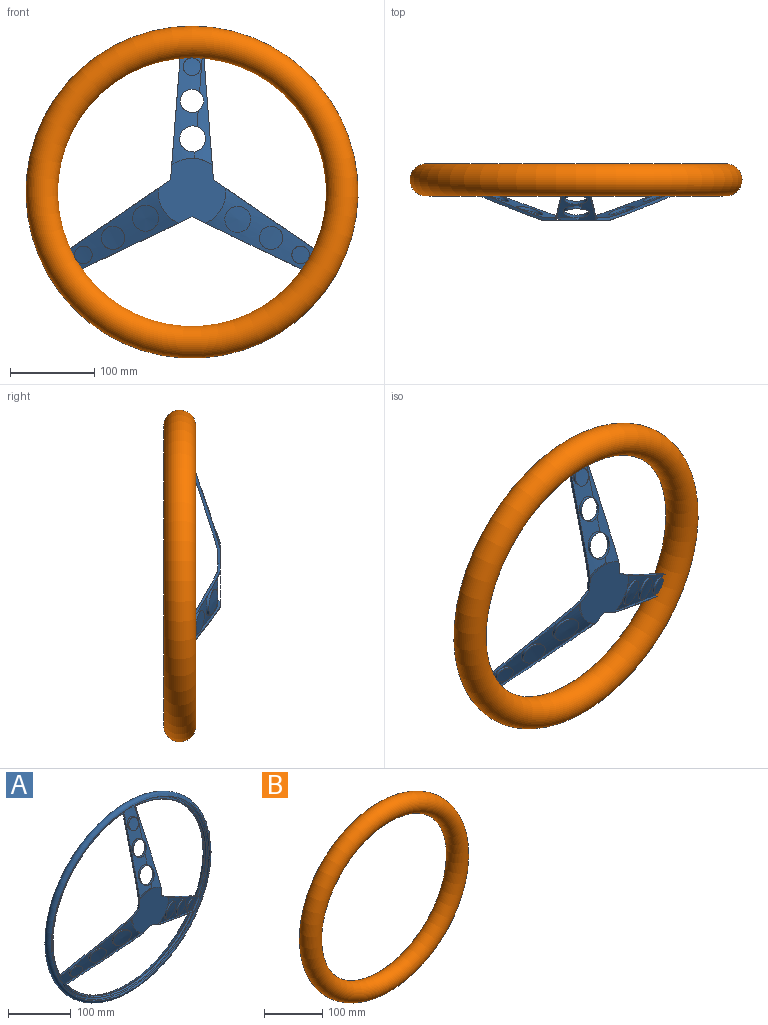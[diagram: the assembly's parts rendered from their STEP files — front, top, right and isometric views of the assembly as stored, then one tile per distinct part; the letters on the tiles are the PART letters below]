
ASSEMBLY  parts=2 mates=1
PART A: 36 faces, bbox 399.2x57.2x399.2 mm
  f0: cone r=178.42mm half-angle=70.8deg, axis (0,1,0), area 1142.8mm2, adj f1,f2,f3,f4,f5,f6
  f1: cone r=183.59mm half-angle=4.7deg, axis (0,-1,0), area 4385.1mm2, adj f0,f7
  f2: cone r=178.42mm half-angle=70.8deg, axis (0,1,0), area 81386.5mm2, adj f0,f3,f4,f5,f8,f9,f10,f11
  f3: cylinder r=13.74mm len=27.48mm, axis (0,1,0), area 302.1mm2, adj f0,f2,f18
  f4: cylinder r=15.35mm len=30.7mm, axis (0,1,0), area 337.5mm2, adj f0,f2,f18
  f5: cone r=40.03mm half-angle=43.4deg, axis (0,-1,0), area 5mm2, adj f0,f2,f6,f8,f19
  f6: plane 158.18x49.64mm, normal (-1,0,-0.08), area 548.4mm2, adj f0,f5,f16,f17,f18,f19,f20
  f7: torus R=178.03mm, axis (0,-1,0), area 32931.8mm2, adj f1,f21
  f8: plane 158.18x49.64mm, normal (1,0,-0.08), area 548.4mm2, adj f2,f5,f9,f10,f18,f19,f20
  f9: torus R=178.03mm, axis (0,-1,0), area 1128mm2, adj f2,f8,f10,f18
  f10: plane 130.84x89.78mm, normal (0.57,0,-0.82), area 548.4mm2, adj f2,f8,f9,f11,f18,f19,f20
  f11: cone r=40.03mm half-angle=43.4deg, axis (0,-1,0), area 5mm2, adj f2,f10,f12,f19
  f12: plane 143.56x67.87mm, normal (-0.43,0,0.9), area 548.8mm2, adj f2,f11,f13,f14,f18,f19,f20
  f13: torus R=178.03mm, axis (0,-1,0), area 1130.4mm2, adj f2,f12,f14,f18
  f14: plane 143.15x68.46mm, normal (0.43,0,0.9), area 548.4mm2, adj f2,f12,f13,f15,f18,f19,f20
  f15: cone r=40.03mm half-angle=43.4deg, axis (0,-1,0), area 5mm2, adj f2,f14,f16,f19
  f16: plane 130.84x89.78mm, normal (-0.57,0,-0.82), area 548.4mm2, adj f2,f6,f15,f17,f18,f19,f20
  f17: torus R=178.03mm, axis (0,-1,0), area 1128mm2, adj f2,f6,f16,f18
  f18: cone r=175.31mm half-angle=70.8deg, axis (0,1,0), area 14493.7mm2, adj f3,f4,f6,f8,f9,f10,f12,f13
  f19: plane 80.2x76.97mm, normal (0,1,0), area 4488.5mm2, adj f5,f6,f8,f10,f11,f12,f14,f15
  f20: plane 78.43x75.57mm, normal (0,-1,0), area 4351.5mm2, adj f6,f8,f10,f12,f14,f16,f18
  f21: plane 350.62x350.62mm, normal (0,1,0), area 3955.8mm2, adj f7,f18
  f22: cylinder r=10.42mm len=20.85mm, axis (0,1,0), area 229.2mm2, adj f18,f29
  f23: cylinder r=15.35mm len=30.7mm, axis (0,1,0), area 337.5mm2, adj f18,f30
  f24: cylinder r=13.74mm len=27.48mm, axis (0,1,0), area 301.9mm2, adj f18,f31
  f25: cylinder r=10.42mm len=20.85mm, axis (0,1,0), area 229.3mm2, adj f18,f32
  f26: cylinder r=15.35mm len=30.7mm, axis (0,1,0), area 337.5mm2, adj f18,f33
  f27: cylinder r=13.74mm len=27.48mm, axis (0,1,0), area 302.1mm2, adj f18,f34
  f28: cylinder r=10.42mm len=20.85mm, axis (0,1,0), area 229.2mm2, adj f18,f35
  f29: cone r=178.42mm half-angle=70.8deg, axis (0,1,0), area 361.6mm2, adj f22
  f30: cone r=178.42mm half-angle=70.8deg, axis (0,1,0), area 784.1mm2, adj f23
  f31: cone r=178.42mm half-angle=70.8deg, axis (0,1,0), area 628.1mm2, adj f24
  f32: cone r=178.42mm half-angle=70.8deg, axis (0,1,0), area 361.4mm2, adj f25
  f33: cone r=178.42mm half-angle=70.8deg, axis (0,1,0), area 783.8mm2, adj f26
  f34: cone r=178.42mm half-angle=70.8deg, axis (0,1,0), area 628.3mm2, adj f27
  f35: cone r=178.42mm half-angle=70.8deg, axis (0,1,0), area 361.5mm2, adj f28
PART B: 1 faces, bbox 426.1x38.1x426.1 mm
  f0: torus R=177.8mm, axis (0,1,0), area 133717.3mm2
PLACE A t=(86.15,33.11,38.88)mm
PLACE B t=(86.15,30.3,38.88)mm fixed
MATE fastened B.f0 <-> A.f0  axis (0,1,0) through (86.15,30.3,38.88)mm
